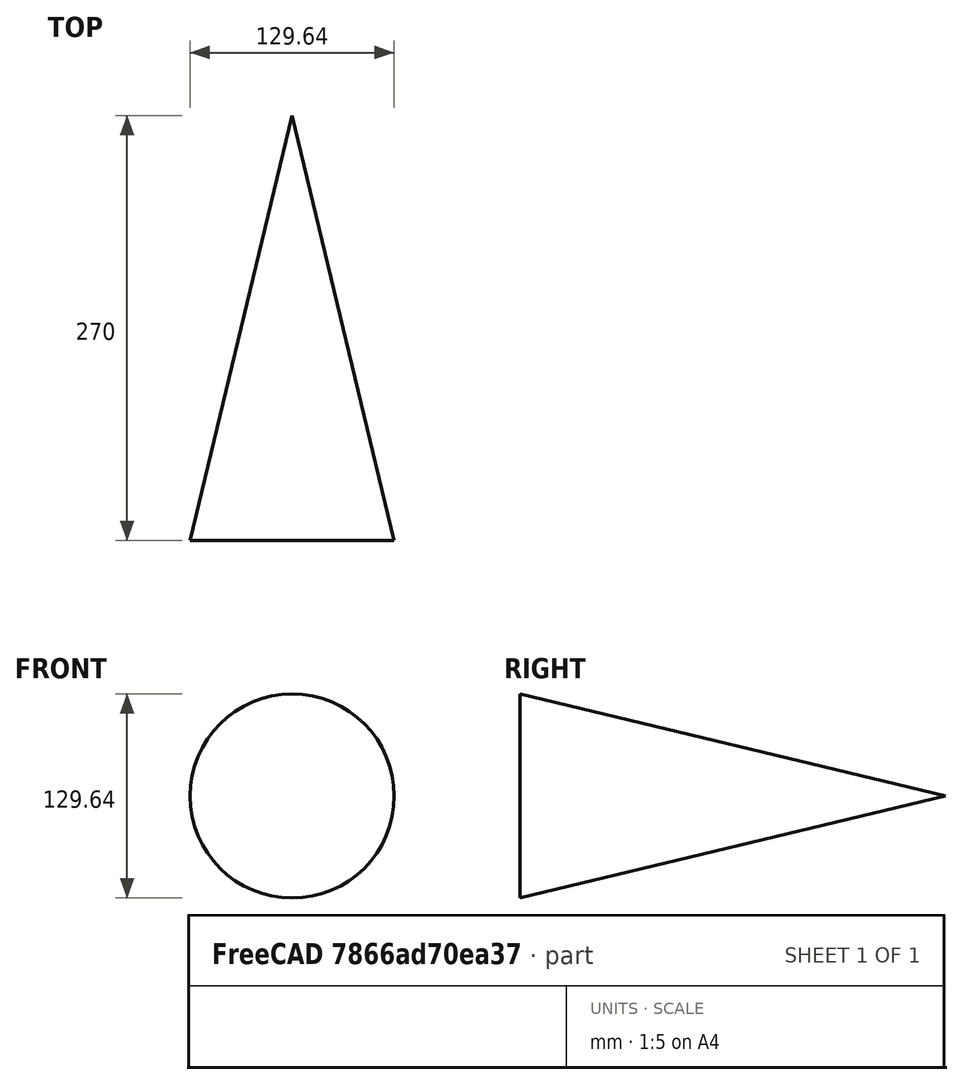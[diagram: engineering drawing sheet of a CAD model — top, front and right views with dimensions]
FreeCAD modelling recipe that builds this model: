
FCSTD DOCUMENT  (FreeCAD 0.20R29177 +426 (Git))
Label: Vl53L0X_ViewCone
License: All rights reserved
LicenseURL: http://en.wikipedia.org/wiki/All_rights_reserved
objects: Sketcher::SketchObject×1, PartDesign::Revolution×1, PartDesign::Body×1, App::Part×1
note: 4 computed .brp shape members not serialized (recipe doc carries the construction recipe); baked Part::Feature solids carry a one-line shape summary decoded from their .brp

FEATURE [Sketcher::SketchObject] Sketch
  FullyConstrained = true
  MapMode = 5
  Placement = pos=(0,0,0) rot=(0.57735,0.57735,0.57735;2.0944rad)
  Support = -> [YZ_Plane001]
  expr: Constraints[6] = 13.5°
  sketch-geometry (3):
    g0: LineSegment StartX=0 StartY=0 StartZ=0 EndX=-270 EndY=64.8213 EndZ=0
    g1: LineSegment StartX=-270 StartY=64.8213 StartZ=0 EndX=-270 EndY=0 EndZ=0
    g2: LineSegment StartX=-270 StartY=0 StartZ=0 EndX=0 EndY=0 EndZ=0
  constraints (8):
    c: Coincident(g0,g-1)
    c: Coincident(g1,g0)
    c: PointOnObject(g1,g-1)
    c: Vertical(g1)
    c: Coincident(g2,g1)
    c: Coincident(g2,g0)
    c: Angle(g0,g2) = 0.235619
    c: DistanceX(g2,g2) = 270
FEATURE [PartDesign::Revolution] Revolution
  Angle = 360
  Axis = (3e-16,1,-2e-16)
  Base = (0,0,0)
  Placement = pos=(0,0,0) rot=(0.57735,0.57735,0.57735;2.0944rad)
  Profile = -> Sketch
  ReferenceAxis = -> Sketch [H_Axis]
FEATURE [PartDesign::Body] Body  label="ViewCone"
  Group = -> [Sketch,Revolution]
  Origin = -> Origin001
  Tip = -> Revolution
FEATURE [App::Part] Part  label="V153L0X_ViewCone"
  Group = -> [Body]
  Origin = -> Origin
